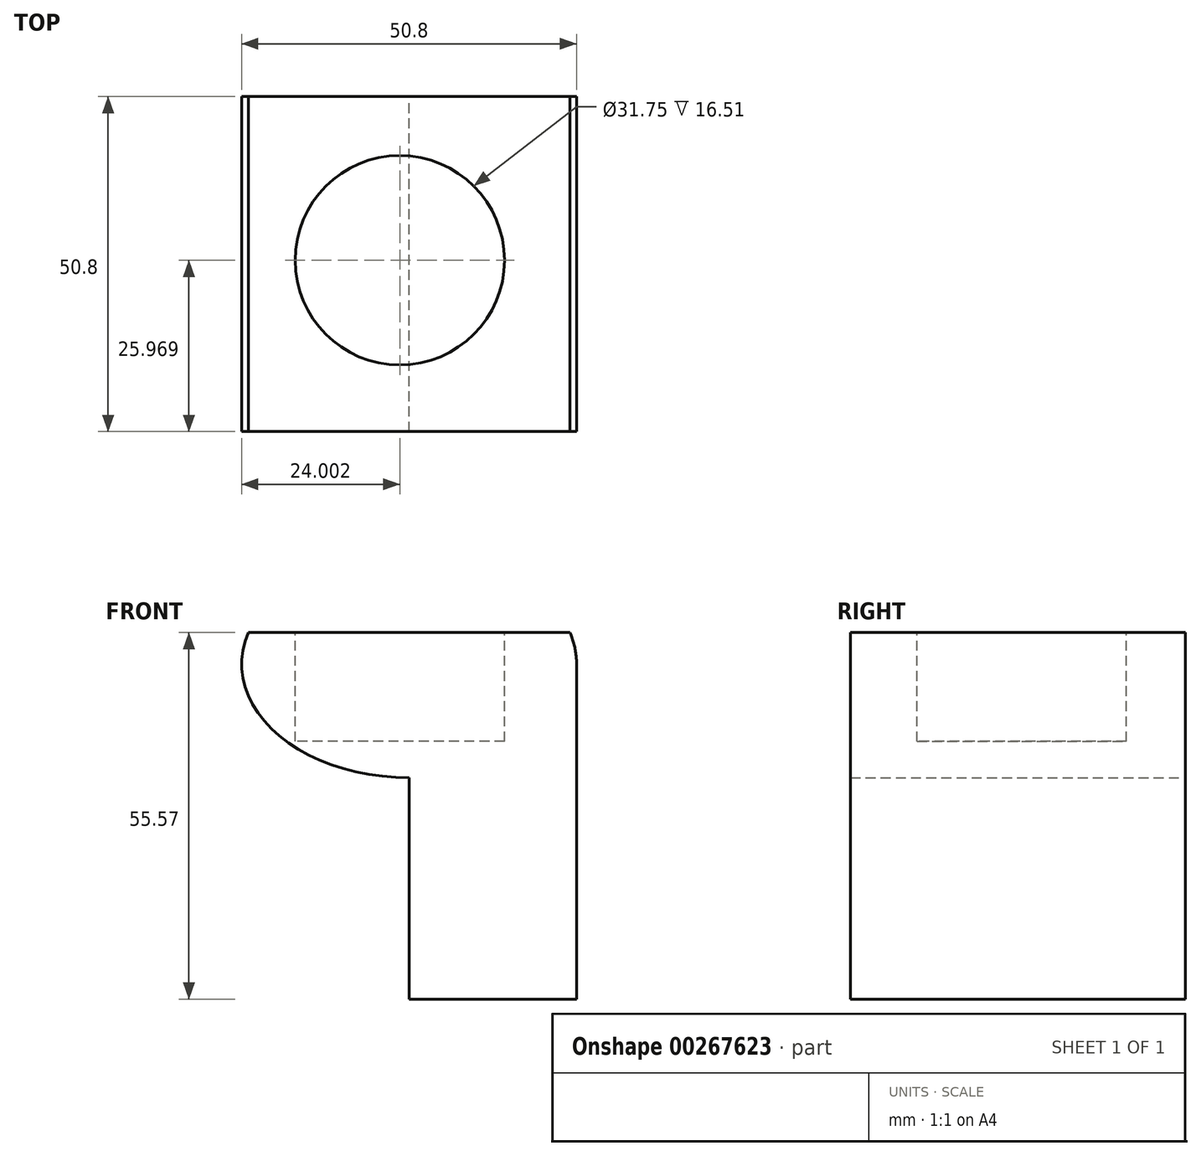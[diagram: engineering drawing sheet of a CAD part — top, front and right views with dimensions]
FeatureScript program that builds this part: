
annotation { "Feature Type Name" : "Feature", "Feature Type Description" : "" }
export const myFeature = defineFeature(function(context is Context, id is Id, definition is map)
    precondition{}
    {
        {
            var Q0;
            Q0=qCreatedBy(makeId("Front.planeOp"),FACE);
            var sketch = newSketch(context, id + "F0", { "sketchPlane" : qUnion([Q0])});
            skLineSegment(sketch, "E0.bottom", {"start": v(33.52, -4.77) * mm, "end": v(58.92, -4.77) * mm});
            skLineSegment(sketch, "E0.top", {"start": v(33.52, -55.57) * mm, "end": v(58.92, -55.57) * mm});
            skLineSegment(sketch, "E0.left", {"start": v(33.52, -4.77) * mm, "end": v(33.52, -55.57) * mm});
            skLineSegment(sketch, "E0.right", {"start": v(58.92, -4.77) * mm, "end": v(58.92, -55.57) * mm});
            skEllipse(sketch, "E1", {"center": v(33.52, -4.77) * mm, "majorRadius": 25.4 * mm, "minorRadius": 17.23 * mm, "majorAxis": v(1, 0)});
            skLineSegment(sketch, "E2", {"start": v(6.5, 0) * mm, "end": v(61.29, 0) * mm});
            skSolve(sketch);
        }
        {
            var Q0;
            {var subQ5=sQuery(id+"F0.wireOp",EDGE,"E0.bottom");Q0=makeQuery(id+"F0.imprint","IMPRINT",FACE,{"disambiguationData":[TD([[makeQuery(id+"F0.imprint","IMPRINT",EDGE,{"derivedFrom":subQ5}),1.0]])]});}
            var Q1;
            {var subQ0=sQuery(id+"F0.wireOp",EDGE,"E0.bottom");Q1=makeQuery(id+"F0.imprint","IMPRINT",FACE,{"disambiguationData":[TD([[makeQuery(id+"F0.imprint","IMPRINT",EDGE,{"derivedFrom":subQ0}),-1.0]])]});}
            var Q2;
            {var subQ0=sQuery(id+"F0.wireOp",EDGE,"E0.top");Q2=makeQuery(id+"F0.imprint","IMPRINT",FACE,{"disambiguationData":[TD([[makeQuery(id+"F0.imprint","IMPRINT",EDGE,{"derivedFrom":subQ0}),1.0]])]});}
            extrude(context, id + "F1", {"entities" : qUnion([Q0, Q1, Q2]), "depth" : 50.8 * mm});
        }
        {
            var Q0;
            Q0=qCreatedBy(makeId("Top.planeOp"),FACE);
            var sketch = newSketch(context, id + "F2", { "sketchPlane" : qUnion([Q0])});
            skCircle(sketch, "E3", {"center": v(32.12, -24.83) * mm, "radius": 15.88 * mm});
            skSolve(sketch);
        }
        {
            var Q0;
            Q0=makeQuery(id+"F2.imprint","IMPRINT",FACE,{"disambiguationData":[TD([[makeQuery(id+"F2.imprint","IMPRINT",EDGE,{"derivedFrom":sQuery(id+"F2.wireOp",EDGE,"E3")}),1.0]])]});
            extrude(context, id + "F3", {"entities" : qUnion([Q0]), "operationType" : NewBodyOperationType.REMOVE, "oppositeDirection" : true, "depth" : 16.5 * mm});
        }
    });
